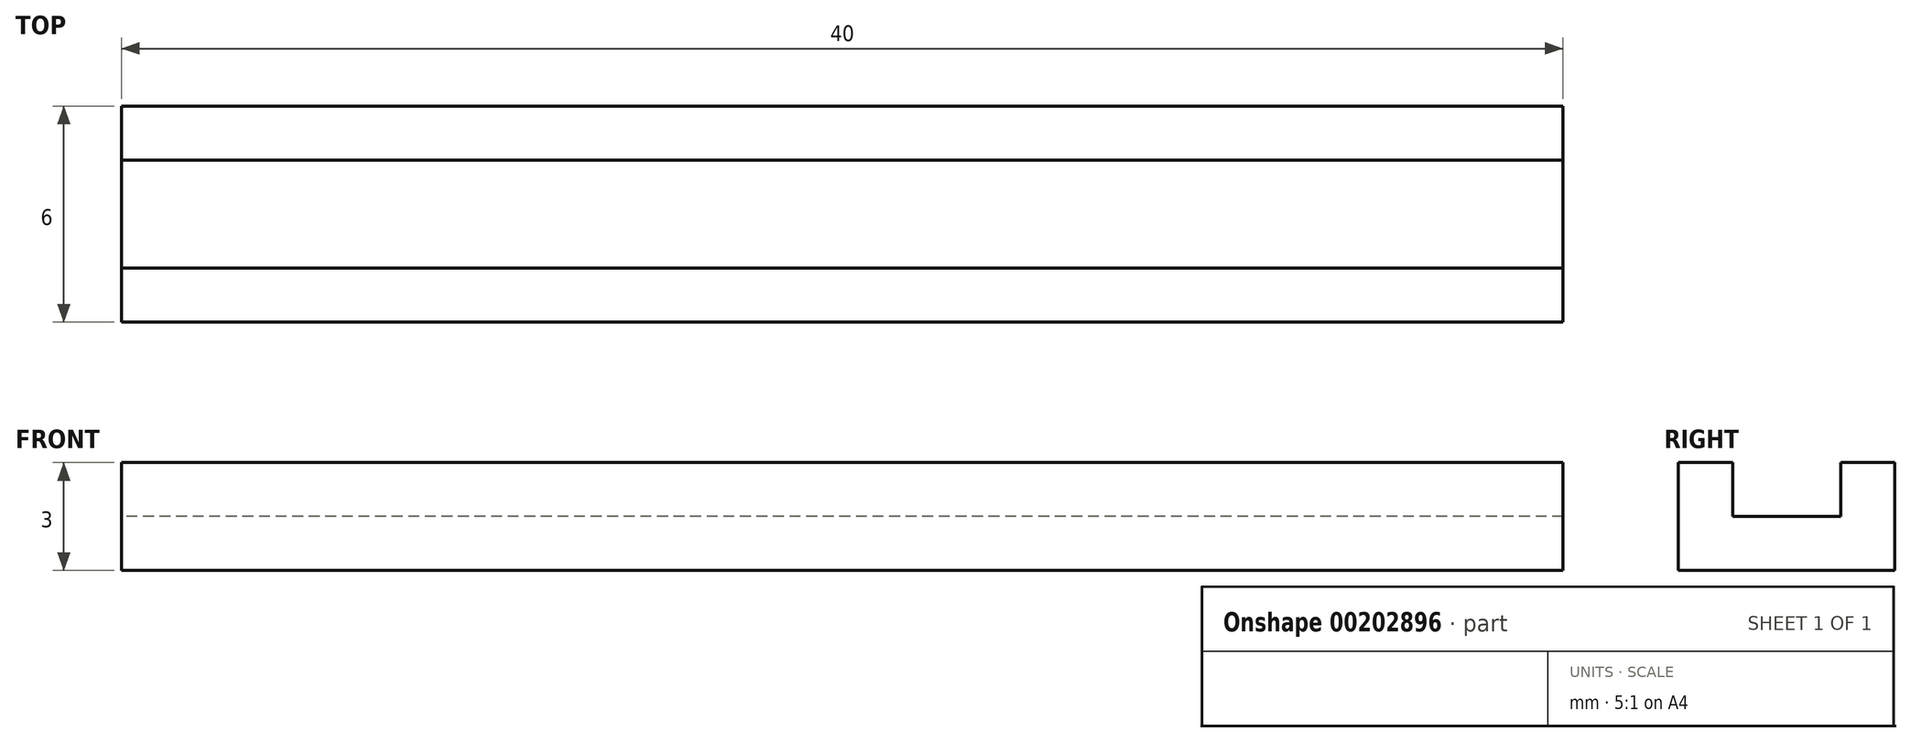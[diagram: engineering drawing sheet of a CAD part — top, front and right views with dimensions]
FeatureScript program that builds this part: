
annotation { "Feature Type Name" : "Feature", "Feature Type Description" : "" }
export const myFeature = defineFeature(function(context is Context, id is Id, definition is map)
    precondition{}
    {
        {
            var Q0;
            Q0=qCreatedBy(makeId("Right.planeOp"),FACE);
            var sketch = newSketch(context, id + "F0", { "sketchPlane" : qUnion([Q0])});
            skLineSegment(sketch, "E0", {"start": v(-4.63, 0) * mm, "end": v(7.64, 0) * mm, "construction": true});
            skLineSegment(sketch, "E1", {"start": v(0, 6.92) * mm, "end": v(0, -6.64) * mm, "construction": true});
            skLineSegment(sketch, "E2", {"start": v(-3, 3) * mm, "end": v(-3, 0) * mm});
            skLineSegment(sketch, "E3", {"start": v(-3, 0) * mm, "end": v(0, 0) * mm});
            skLineSegment(sketch, "E4", {"start": v(-3, 3) * mm, "end": v(-1.5, 3) * mm});
            skLineSegment(sketch, "E5", {"start": v(-1.5, 3) * mm, "end": v(-1.5, 1.5) * mm});
            skLineSegment(sketch, "E6", {"start": v(-1.5, 1.5) * mm, "end": v(0, 1.5) * mm});
            skLineSegment(sketch, "E7.MirrorCS", {"start": v(1.5, 3) * mm, "end": v(1.5, 1.5) * mm});
            skLineSegment(sketch, "E8.MirrorCS", {"start": v(1.5, 1.5) * mm, "end": v(0, 1.5) * mm});
            skLineSegment(sketch, "E9.MirrorCS", {"start": v(3, 3) * mm, "end": v(1.5, 3) * mm});
            skLineSegment(sketch, "E10.MirrorCS", {"start": v(3, 3) * mm, "end": v(3, 0) * mm});
            skLineSegment(sketch, "E11.MirrorCS", {"start": v(3, 0) * mm, "end": v(0, 0) * mm});
            skSolve(sketch);
        }
        {
            var Q0;
            Q0=qSketchRegion(id+"F0",true);
            extrude(context, id + "F1", {"entities" : qUnion([Q0]), "depth" : 40 * mm});
        }
    });
